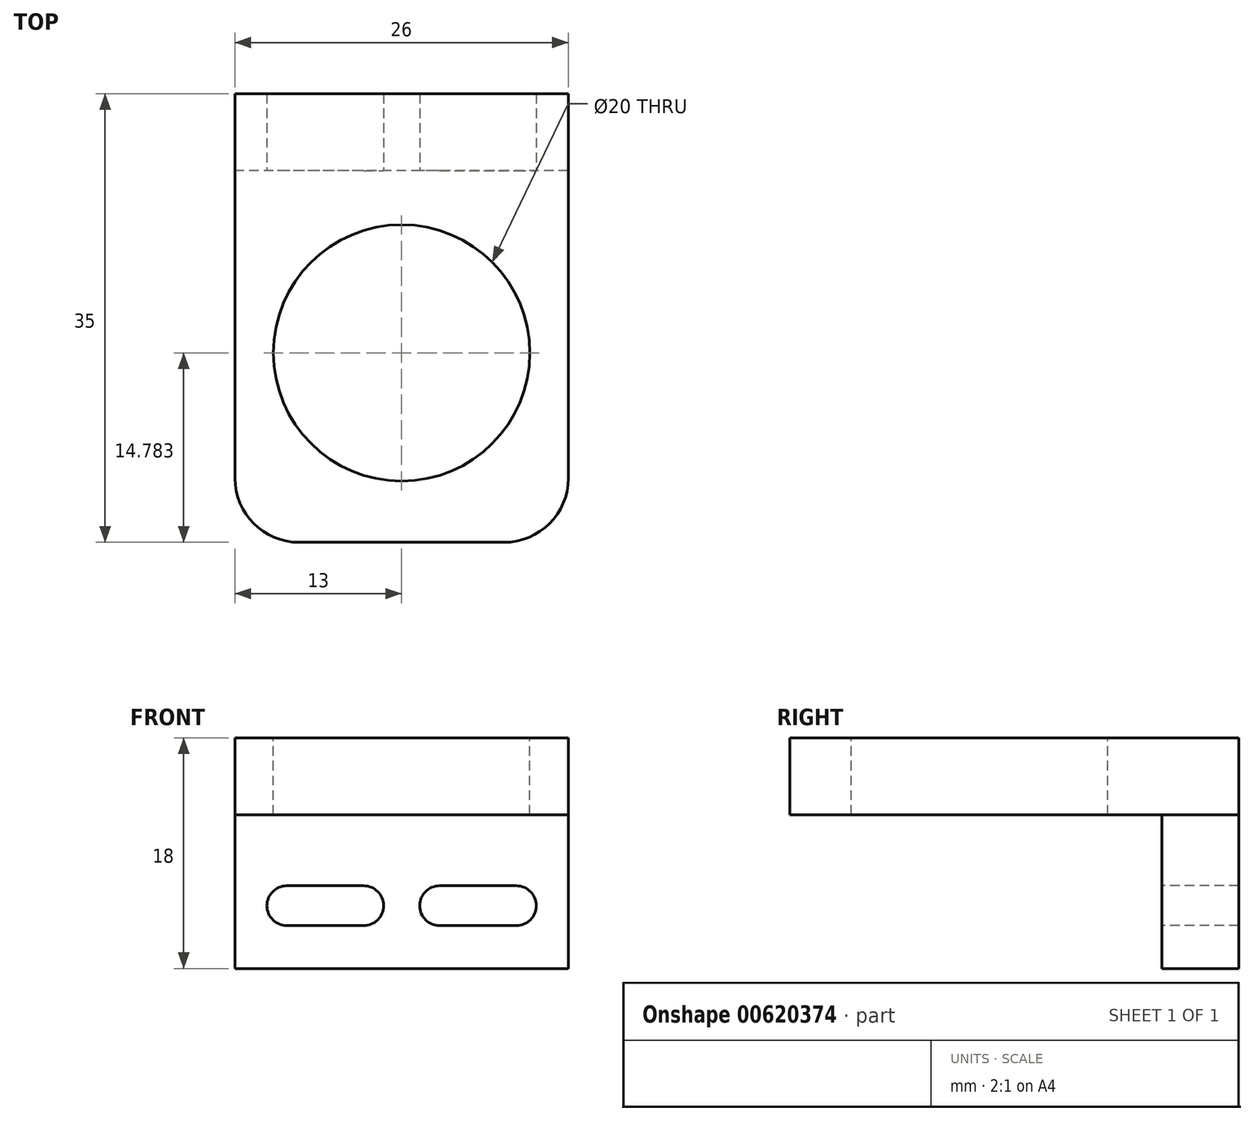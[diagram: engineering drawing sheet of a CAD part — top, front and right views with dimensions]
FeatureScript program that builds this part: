
annotation { "Feature Type Name" : "Feature", "Feature Type Description" : "" }
export const myFeature = defineFeature(function(context is Context, id is Id, definition is map)
    precondition{}
    {
        {
            var Q0;
            Q0=qCreatedBy(makeId("Front.planeOp"),FACE);
            var sketch = newSketch(context, id + "F0", { "sketchPlane" : qUnion([Q0])});
            skLineSegment(sketch, "E0.bottom", {"start": v(-13, 15) * mm, "end": v(13, 15) * mm});
            skLineSegment(sketch, "E0.top", {"start": v(-13, -15) * mm, "end": v(13, -15) * mm});
            skLineSegment(sketch, "E0.left", {"start": v(-13, 15) * mm, "end": v(-13, -15) * mm});
            skLineSegment(sketch, "E0.right", {"start": v(13, 15) * mm, "end": v(13, -15) * mm});
            skPoint(sketch, "E0.middle", {"position": v(0, 0) * mm});
            skSolve(sketch);
        }
        {
            var Q0;
            Q0=makeQuery(id+"F0.imprint","IMPRINT",FACE,{"disambiguationData":[TD([[makeQuery(id+"F0.imprint","IMPRINT",EDGE,{"derivedFrom":sQuery(id+"F0.wireOp",EDGE,"E0.bottom")}),-1.0]])]});
            var sketch = newSketch(context, id + "F1", { "sketchPlane" : qUnion([Q0])});
            skLineSegment(sketch, "E1.bottom", {"start": v(13, -3) * mm, "end": v(-13, -3) * mm});
            skLineSegment(sketch, "E1.top", {"start": v(13, 3) * mm, "end": v(-13, 3) * mm});
            skLineSegment(sketch, "E1.left", {"start": v(13, -3) * mm, "end": v(13, 3) * mm});
            skLineSegment(sketch, "E1.right", {"start": v(-13, -3) * mm, "end": v(-13, 3) * mm});
            skPoint(sketch, "E1.middle", {"position": v(0, 0) * mm});
            skSolve(sketch);
        }
        {
            var Q0;
            Q0=makeQuery(id+"F1.imprint","IMPRINT",FACE,{"disambiguationData":[TD([[makeQuery(id+"F1.imprint","IMPRINT",EDGE,{"derivedFrom":sQuery(id+"F1.wireOp",EDGE,"E1.bottom")}),-1.0]])]});
            extrude(context, id + "F2", {"entities" : qUnion([Q0]), "depth" : 35 * mm, "offsetDistance" : 25 * mm});
        }
        {
            var Q0;
            {var subQ0=sQuery(id+"F1.wireOp",EDGE,"E1.bottom");Q0=makeQuery(id+"F1.imprint","IMPRINT",FACE,{"disambiguationData":[TD([[makeQuery(id+"F1.imprint","IMPRINT",EDGE,{"derivedFrom":subQ0}),1.0]])]});}
            extrude(context, id + "F3", {"entities" : qUnion([Q0]), "depth" : 6 * mm, "offsetDistance" : 25 * mm});
        }
        {
            var Q0;
            Q0=makeQuery(id+"F2.opExtrude","SWEPT_FACE",FACE,{"disambiguationData":[OSD([sQuery(id+"F1.wireOp",EDGE,"E1.top")])]});
            var sketch = newSketch(context, id + "F4", { "sketchPlane" : qUnion([Q0])});
            skCircle(sketch, "E2", {"center": v(0, -20.22) * mm, "radius": 10 * mm});
            skPoint(sketch, "E2.centerSnap0", {"position": v(0, -35) * mm});
            skSolve(sketch);
        }
        {
            var Q0;
            Q0=makeQuery(id+"F3.opExtrude","CAP_FACE",FACE,{"disambiguationData":[OSD([sQuery(id+"F0.wireOp",EDGE,"E0.top"),sQuery(id+"F0.wireOp",EDGE,"E0.left"),sQuery(id+"F0.wireOp",EDGE,"E0.right"),sQuery(id+"F1.wireOp",EDGE,"E1.bottom")])],"isStart":false});
            var sketch = newSketch(context, id + "F5", { "sketchPlane" : qUnion([Q0])});
            skLineSegment(sketch, "E3", {"start": v(0, -3.61) * mm, "end": v(0, -14.45) * mm});
            skPoint(sketch, "E3.startSnap0", {"position": v(0, -3) * mm});
            skPoint(sketch, "E4.MirrorCS.end.orphan", {"position": v(5.47, -8.55) * mm});
            skPoint(sketch, "E5.end.orphan", {"position": v(-5.47, -8.55) * mm});
            skPoint(sketch, "E6.MirrorCS.start.orphan", {"position": v(5.5, -11.45) * mm});
            skPoint(sketch, "E7.MirrorCS.start.orphan", {"position": v(5.5, -8.55) * mm});
            skPoint(sketch, "E8.start.orphan", {"position": v(-5.5, -11.45) * mm});
            skPoint(sketch, "E9.start.orphan", {"position": v(-5.5, -8.55) * mm});
            skLineSegment(sketch, "E10", {"start": v(8.96, -8.55) * mm, "end": v(8.96, -8.55) * mm});
            skPoint(sketch, "E11.MirrorCS.start.orphan", {"position": v(9.5, -8.45) * mm});
            skPoint(sketch, "E12.start.orphan", {"position": v(8.96, -11.45) * mm});
            skLineSegment(sketch, "E13", {"start": v(2.96, -11.65) * mm, "end": v(8.96, -11.65) * mm});
            skArc(sketch, "E14", {"start": v(2.96, -11.65) * mm, "mid": v(1.4, -10.1) * mm, "end": v(2.96, -8.55) * mm});
            skLineSegment(sketch, "E15", {"start": v(5.47, -8.55) * mm, "end": v(5.5, -8.55) * mm});
            skLineSegment(sketch, "E16", {"start": v(5.5, -8.55) * mm, "end": v(5.47, -8.55) * mm});
            skLineSegment(sketch, "E17", {"start": v(2.96, -8.55) * mm, "end": v(8.96, -8.55) * mm});
            skArc(sketch, "E18", {"start": v(8.96, -11.65) * mm, "mid": v(10.5, -10.1) * mm, "end": v(8.96, -8.55) * mm});
            skPoint(sketch, "E19.end.orphan", {"position": v(-8.96, -11.45) * mm});
            skPoint(sketch, "E19.start.orphan", {"position": v(-9.5, -8.45) * mm});
            skLineSegment(sketch, "E20.MirrorCS", {"start": v(-5.47, -8.55) * mm, "end": v(-5.5, -8.55) * mm});
            skLineSegment(sketch, "E21.MirrorCS", {"start": v(-5.5, -8.55) * mm, "end": v(-5.47, -8.55) * mm});
            skLineSegment(sketch, "E22.MirrorCS", {"start": v(-8.96, -8.55) * mm, "end": v(-8.96, -8.55) * mm});
            skLineSegment(sketch, "E23.MirrorCS", {"start": v(-2.96, -11.65) * mm, "end": v(-8.96, -11.65) * mm});
            skArc(sketch, "E24.MirrorCS", {"start": v(-8.96, -11.65) * mm, "mid": v(-10.5, -10.1) * mm, "end": v(-8.96, -8.55) * mm});
            skLineSegment(sketch, "E25.MirrorCS", {"start": v(-2.96, -8.55) * mm, "end": v(-8.96, -8.55) * mm});
            skArc(sketch, "E26.MirrorCS", {"start": v(-2.96, -11.65) * mm, "mid": v(-1.4, -10.1) * mm, "end": v(-2.96, -8.55) * mm});
            skSolve(sketch);
        }
        {
            var Q0;
            Q0 = qSketchRegion(id + "F5", true);
            extrude(context, id + "F6", {"entities" : qUnion([Q0]), "operationType" : NewBodyOperationType.REMOVE, "endBound" : BoundingType.THROUGH_ALL, "oppositeDirection" : true, "depth" : 25 * mm, "offsetDistance" : 25 * mm});
        }
        {
            var Q0;
            Q0 = qSketchRegion(id + "F4", true);
            extrude(context, id + "F7", {"entities" : qUnion([Q0]), "operationType" : NewBodyOperationType.REMOVE, "endBound" : BoundingType.THROUGH_ALL, "oppositeDirection" : true, "depth" : 25 * mm, "offsetDistance" : 25 * mm});
        }
        {
            var Q0;
            Q0=makeQuery(id+"F2.opExtrude","CAP_EDGE",EDGE,{"disambiguationData":[OSD([sQuery(id+"F1.wireOp",EDGE,"E1.right")])],"isStart":false});
            var Q1;
            Q1=makeQuery(id+"F2.opExtrude","CAP_EDGE",EDGE,{"disambiguationData":[OSD([sQuery(id+"F1.wireOp",EDGE,"E1.left")])],"isStart":false});
            fillet(context, id + "F8", {"entities" : qUnion([Q0, Q1]), "radius" : 5 * mm, "tangentPropagation" : true, "allowEdgeOverflow" : false});
        }
    });
